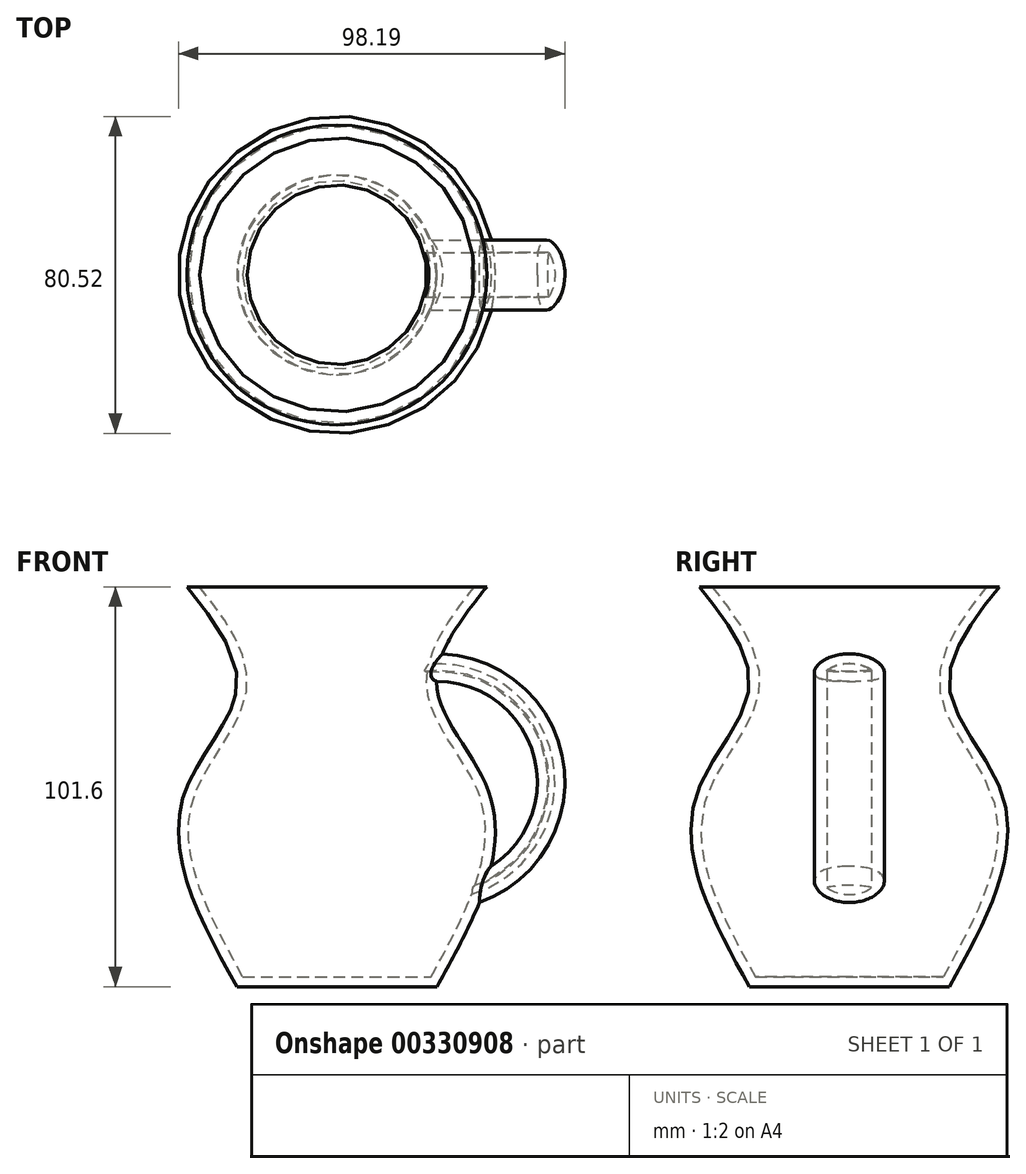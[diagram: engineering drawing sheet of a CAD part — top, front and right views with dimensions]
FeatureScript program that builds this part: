
annotation { "Feature Type Name" : "Feature", "Feature Type Description" : "" }
export const myFeature = defineFeature(function(context is Context, id is Id, definition is map)
    precondition{}
    {
        {
            var Q0;
            Q0=qCreatedBy(makeId("Top.planeOp"),FACE);
            cPlane(context, id + "F0", {"entities" : qUnion([Q0]), "cplaneType" : CPlaneType.OFFSET, "offset" : 50.8 * mm, "oppositeDirection" : true, "width" : 152.4 * mm, "height" : 152.4 * mm});
        }
        {
            var Q0;
            Q0=qCreatedBy(id+"F0.planeOp",FACE);
            var sketch = newSketch(context, id + "F1", { "sketchPlane" : qUnion([Q0])});
            skCircle(sketch, "E0", {"center": v(0, 0) * mm, "radius": 25.4 * mm});
            skSolve(sketch);
        }
        {
            var Q0;
            Q0=qCreatedBy(makeId("Top.planeOp"),FACE);
            var sketch = newSketch(context, id + "F2", { "sketchPlane" : qUnion([Q0])});
            skCircle(sketch, "E1", {"center": v(0, 0) * mm, "radius": 38.1 * mm});
            skSolve(sketch);
        }
        {
            var Q0;
            Q0=qCreatedBy(makeId("Top.planeOp"),FACE);
            cPlane(context, id + "F3", {"entities" : qUnion([Q0]), "cplaneType" : CPlaneType.OFFSET, "offset" : 25.4 * mm, "width" : 152.4 * mm, "height" : 152.4 * mm});
        }
        {
            var Q0;
            Q0=qCreatedBy(id+"F3.planeOp",FACE);
            var sketch = newSketch(context, id + "F4", { "sketchPlane" : qUnion([Q0])});
            skCircle(sketch, "E2", {"center": v(0, 0) * mm, "radius": 25.4 * mm});
            skSolve(sketch);
        }
        {
            var Q0;
            Q0=qCreatedBy(makeId("Top.planeOp"),FACE);
            cPlane(context, id + "F5", {"entities" : qUnion([Q0]), "cplaneType" : CPlaneType.OFFSET, "offset" : 50.8 * mm, "width" : 152.4 * mm, "height" : 152.4 * mm});
        }
        {
            var Q0;
            Q0=qCreatedBy(id+"F5.planeOp",FACE);
            var sketch = newSketch(context, id + "F6", { "sketchPlane" : qUnion([Q0])});
            skCircle(sketch, "E3", {"center": v(0, 0) * mm, "radius": 38.1 * mm});
            skSolve(sketch);
        }
        {
            var Q0;
            Q0=makeQuery(id+"F1.imprint","IMPRINT",FACE,{"disambiguationData":[TD([[makeQuery(id+"F1.imprint","IMPRINT",EDGE,{"derivedFrom":sQuery(id+"F1.wireOp",EDGE,"E0")}),1.0]])]});
            var Q1;
            Q1=makeQuery(id+"F2.imprint","IMPRINT",FACE,{"disambiguationData":[TD([[makeQuery(id+"F2.imprint","IMPRINT",EDGE,{"derivedFrom":sQuery(id+"F2.wireOp",EDGE,"E1")}),1.0]])]});
            var Q2;
            Q2=makeQuery(id+"F4.imprint","IMPRINT",FACE,{"disambiguationData":[TD([[makeQuery(id+"F4.imprint","IMPRINT",EDGE,{"derivedFrom":sQuery(id+"F4.wireOp",EDGE,"E2")}),1.0]])]});
            var Q3;
            Q3=makeQuery(id+"F6.imprint","IMPRINT",FACE,{"disambiguationData":[TD([[makeQuery(id+"F6.imprint","IMPRINT",EDGE,{"derivedFrom":sQuery(id+"F6.wireOp",EDGE,"E3")}),1.0]])]});
            loft(context, id + "F7", {"sheetProfilesArray" : [{ "sheetProfileEntities" : qUnion([Q0]) }, { "sheetProfileEntities" : qUnion([Q1]) }, { "sheetProfileEntities" : qUnion([Q2]) }, { "sheetProfileEntities" : qUnion([Q3]) }]});
        }
        {
            var Q0;
            Q0=qCreatedBy(makeId("Right.planeOp"),FACE);
            var sketch = newSketch(context, id + "F8", { "sketchPlane" : qUnion([Q0])});
            skCircle(sketch, "E4", {"center": v(0, 12.7) * mm, "radius": 8.9 * mm});
            skLineSegment(sketch, "E5", {"start": v(0, -50.8) * mm, "end": v(0, 50.8) * mm, "construction": true});
            skSolve(sketch);
        }
        {
            var Q0;
            Q0=qCreatedBy(makeId("Front.planeOp"),FACE);
            var sketch = newSketch(context, id + "F9", { "sketchPlane" : qUnion([Q0])});
            skArc(sketch, "E6", {"start": v(0, -10.16) * mm, "mid": v(53.25, 1.27) * mm, "end": v(0, 12.7) * mm});
            skSolve(sketch);
        }
        {
            var Q0;
            Q0=makeQuery(id+"F8.imprint","IMPRINT",FACE,{"disambiguationData":[TD([[makeQuery(id+"F8.imprint","IMPRINT",EDGE,{"derivedFrom":sQuery(id+"F8.wireOp",EDGE,"E4")}),1.0]])]});
            var Q1;
            Q1=sQuery(id+"F9.wireOp",EDGE,"E6");
            sweep(context, id + "F10", {"operationType" : NewBodyOperationType.ADD, "profiles" : qUnion([Q0]), "path" : qUnion([Q1])});
        }
        {
            var Q0;
            Q0=makeQuery(id+"F7.opLoft","CAP_FACE",FACE,{"disambiguationData":[OSD([makeQuery(id+"F6.imprint","IMPRINT",FACE,{"disambiguationData":[TD([[makeQuery(id+"F6.imprint","IMPRINT",EDGE,{"derivedFrom":sQuery(id+"F6.wireOp",EDGE,"E3")}),1.0]])]})])],"isStart":true});
            shell(context, id + "F11", {"entities" : qUnion([Q0]), "thickness" : 2.54 * mm});
        }
    });
